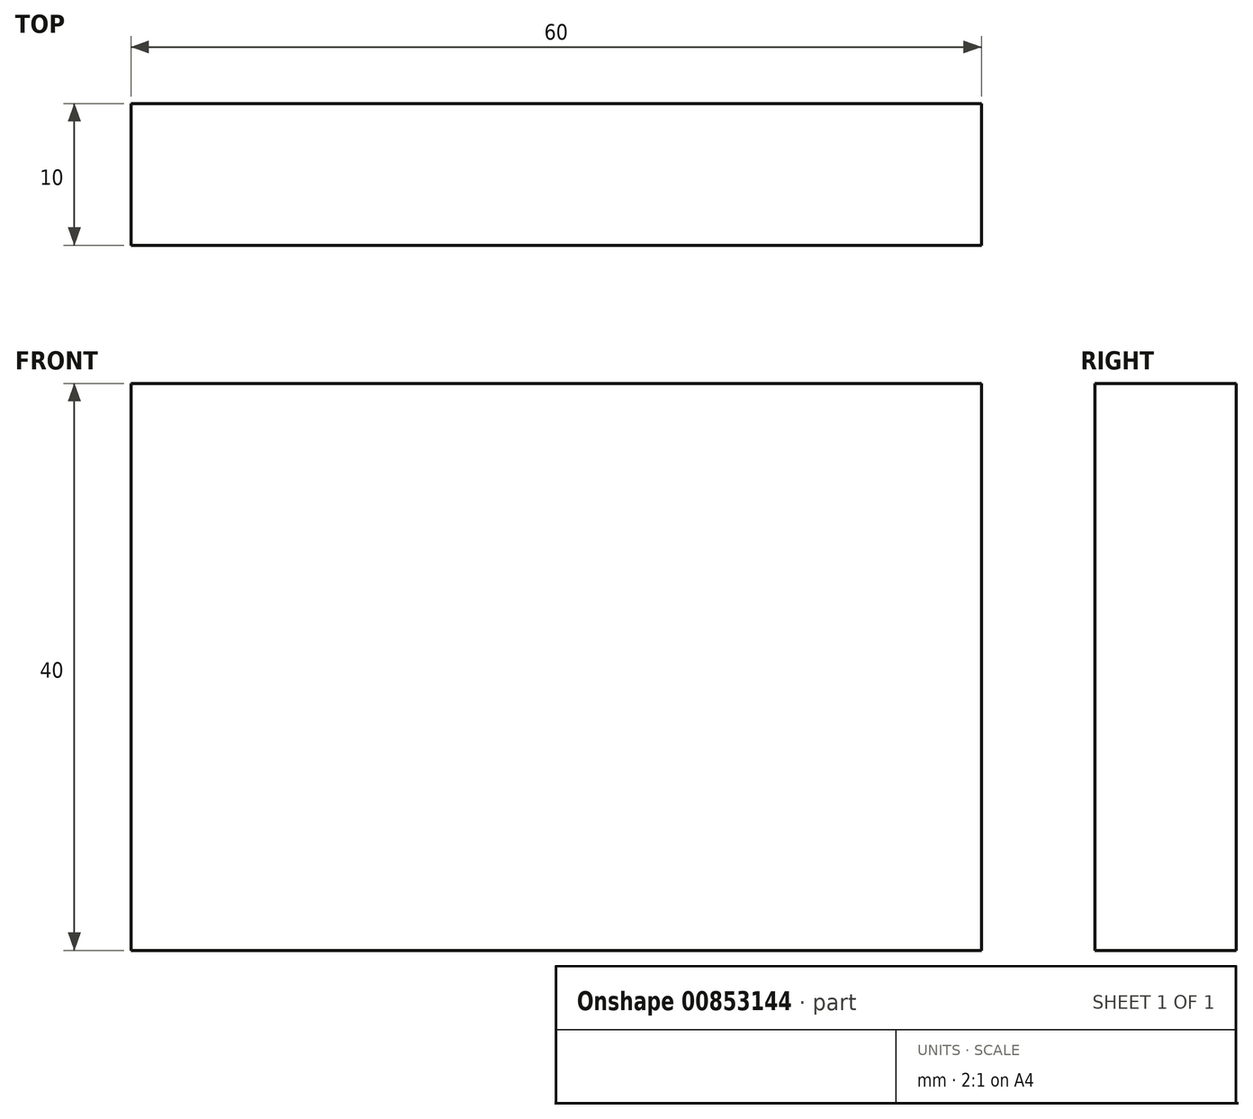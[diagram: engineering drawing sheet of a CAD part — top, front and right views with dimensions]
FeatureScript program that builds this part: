
annotation { "Feature Type Name" : "Feature", "Feature Type Description" : "" }
export const myFeature = defineFeature(function(context is Context, id is Id, definition is map)
    precondition{}
    {
        {
            var Q0;
            Q0=qCreatedBy(makeId("Top.planeOp"),FACE);
            var sketch = newSketch(context, id + "F0", { "sketchPlane" : qUnion([Q0])});
            skLineSegment(sketch, "E0.top", {"start": v(-20, -20) * mm, "end": v(40, -20) * mm});
            skLineSegment(sketch, "E0.left", {"start": v(-20, 0) * mm, "end": v(-20, -20) * mm});
            skLineSegment(sketch, "E0.right", {"start": v(40, -10) * mm, "end": v(40, -20) * mm});
            skCircle(sketch, "E1", {"center": v(0, 0) * mm, "radius": 10 * mm});
            skArc(sketch, "E2", {"start": v(20, 0) * mm, "mid": v(0, 20) * mm, "end": v(-20, 0) * mm});
            skArc(sketch, "E3", {"start": v(40, -10) * mm, "mid": v(37.07, -2.93) * mm, "end": v(30, 0) * mm});
            skLineSegment(sketch, "E4.trimOffspring", {"start": v(20, 0) * mm, "end": v(30, 0) * mm});
            skLineSegment(sketch, "E5.top", {"start": v(-20, -10) * mm, "end": v(40, -10) * mm});
            skLineSegment(sketch, "E5.left", {"start": v(-20, -20) * mm, "end": v(-20, -10) * mm});
            skLineSegment(sketch, "E5.right", {"start": v(40, -20) * mm, "end": v(40, -10) * mm});
            skSolve(sketch);
        }
        {
            var Q0;
            {var subQ2=sQuery(id+"F0.wireOp",EDGE,"E0.left");Q0=makeQuery(id+"F0.imprint","IMPRINT",FACE,{"disambiguationData":[TD([[makeQuery(id+"F0.imprint","IMPRINT",EDGE,{"derivedFrom":subQ2}),1.0]])]});}
            var Q1;
            Q1=makeQuery(id+"F0.imprint","IMPRINT",FACE,{"disambiguationData":[TD([[makeQuery(id+"F0.imprint","IMPRINT",EDGE,{"derivedFrom":sQuery(id+"F0.wireOp",EDGE,"E0.top")}),1.0]])]});
            extrude(context, id + "F1", {"entities" : qUnion([Q0, Q1]), "depth" : 20 * mm, "offsetDistance" : 25 * mm});
        }
        {
            var Q0;
            Q0=makeQuery(id+"F0.imprint","IMPRINT",FACE,{"disambiguationData":[TD([[makeQuery(id+"F0.imprint","IMPRINT",EDGE,{"derivedFrom":sQuery(id+"F0.wireOp",EDGE,"E0.top")}),1.0]])]});
            extrude(context, id + "F2", {"entities" : qUnion([Q0]), "operationType" : NewBodyOperationType.ADD, "depth" : 40 * mm, "offsetDistance" : 25 * mm});
        }
    });
